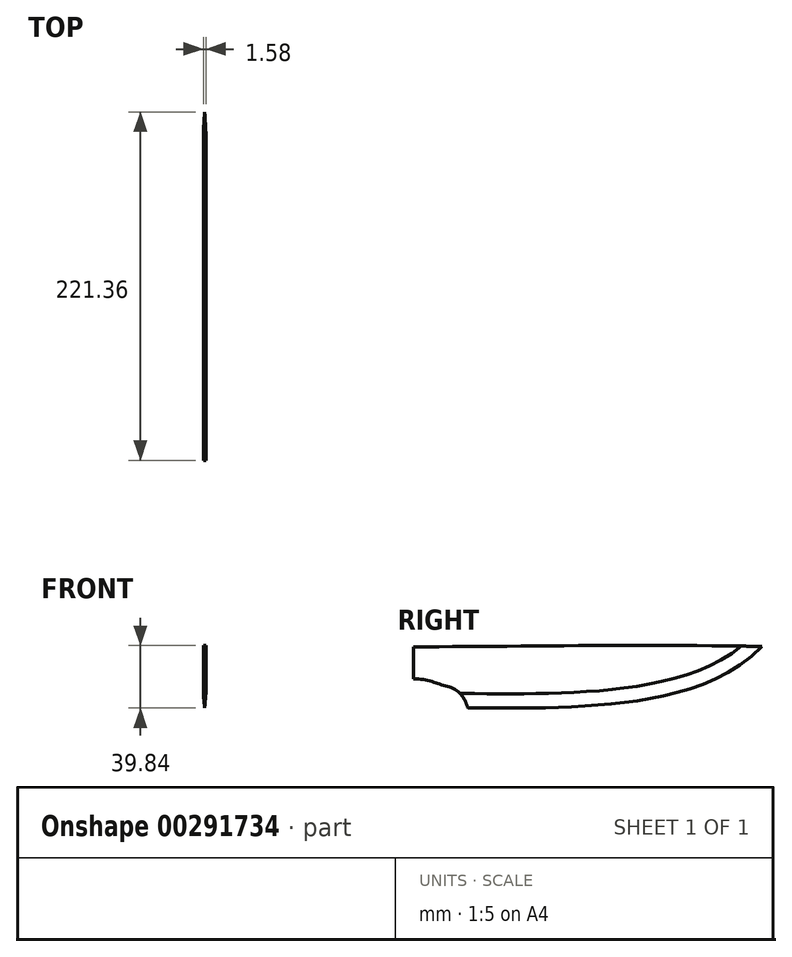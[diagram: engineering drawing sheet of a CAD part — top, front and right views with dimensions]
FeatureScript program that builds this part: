
annotation { "Feature Type Name" : "Feature", "Feature Type Description" : "" }
export const myFeature = defineFeature(function(context is Context, id is Id, definition is map)
    precondition{}
    {
        {
            var Q0;
            Q0=qCreatedBy(makeId("Right.planeOp"),FACE);
            var sketch = newSketch(context, id + "F0", { "sketchPlane" : qUnion([Q0])});
            skLineSegment(sketch, "E0", {"start": v(0, 0) * mm, "end": v(0, -43.94) * mm});
            skFitSpline(sketch, "E1", {"points": [v(0, 0) * mm, v(228.6, 0) * mm], "startDerivative": vector(201.13, 0) * mm, "endDerivative": vector(232.35, -6.13) * mm});
            skFitSpline(sketch, "E2", {"points": [v(0, -43.94) * mm, v(228.6, 0) * mm], "startDerivative": vector(283.14, -1.53) * mm, "endDerivative": vector(131.42, 150.17) * mm});
            skSolve(sketch);
        }
        {
            var Q0;
            Q0 = qSketchRegion(id + "F0", true);
            extrude(context, id + "F1", {"entities" : qUnion([Q0]), "endBound" : BoundingType.SYMMETRIC, "depth" : 1.59 * mm});
        }
        {
            var Q0;
            Q0=makeQuery(id+"F1.opExtrude","CAP_EDGE",EDGE,{"disambiguationData":[OSD([sQuery(id+"F0.wireOp",EDGE,"E2")])],"isStart":true});
            var Q1;
            Q1=makeQuery(id+"F1.opExtrude","CAP_EDGE",EDGE,{"disambiguationData":[OSD([sQuery(id+"F0.wireOp",EDGE,"E2")])],"isStart":false});
            chamfer(context, id + "F2", {"entities" : qUnion([Q0, Q1]), "chamferType" : ChamferType.OFFSET_ANGLE, "width" : 1.27 * mm, "oppositeDirection" : false, "angle" : 85 * degree});
        }
        {
            var Q0;
            Q0=makeQuery(id+"F1.opExtrude","CAP_FACE",FACE,{"disambiguationData":[OSD([sQuery(id+"F0.wireOp",EDGE,"E0"),sQuery(id+"F0.wireOp",EDGE,"E1"),sQuery(id+"F0.wireOp",EDGE,"E2")])],"isStart":true});
            var sketch = newSketch(context, id + "F3", { "sketchPlane" : qUnion([Q0])});
            skFitSpline(sketch, "E3", {"points": [v(0, -20.26) * mm, v(-18.61, -24.3) * mm, v(-34.5, -38.8) * mm], "startDerivative": vector(-47.85, 0.16) * mm, "endDerivative": vector(-22.19, -69.65) * mm});
            skLineSegment(sketch, "E4", {"start": v(-34.5, -38.8) * mm, "end": v(0, -38.8) * mm});
            skLineSegment(sketch, "E5", {"start": v(0, -38.8) * mm, "end": v(0, -20.26) * mm});
            skSolve(sketch);
        }
        {
            var Q0;
            Q0 = qSketchRegion(id + "F3", true);
            extrude(context, id + "F4", {"entities" : qUnion([Q0]), "operationType" : NewBodyOperationType.REMOVE, "endBound" : BoundingType.THROUGH_ALL, "oppositeDirection" : true, "depth" : 25.4 * mm});
        }
    });
